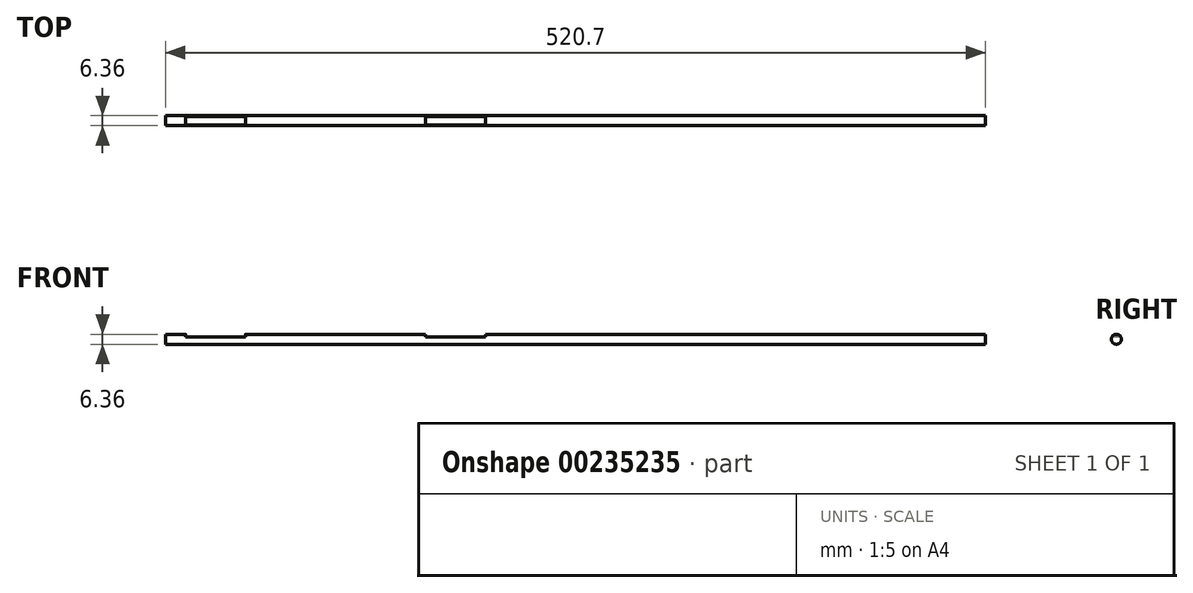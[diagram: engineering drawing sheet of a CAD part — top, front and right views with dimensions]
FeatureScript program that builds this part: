
annotation { "Feature Type Name" : "Feature", "Feature Type Description" : "" }
export const myFeature = defineFeature(function(context is Context, id is Id, definition is map)
    precondition{}
    {
        {
            var Q0;
            Q0=qCreatedBy(makeId("Right.planeOp"),FACE);
            var sketch = newSketch(context, id + "F0", { "sketchPlane" : qUnion([Q0])});
            skCircle(sketch, "E0", {"center": v(0, 0) * mm, "radius": 3.18 * mm});
            skSolve(sketch);
        }
        {
            var Q0;
            Q0=makeQuery(id+"F0.imprint","IMPRINT",FACE,{"disambiguationData":[TD([[makeQuery(id+"F0.imprint","IMPRINT",EDGE,{"derivedFrom":sQuery(id+"F0.wireOp",EDGE,"E0")}),1.0]])]});
            var Q1;
            Q1=sQuery(id+"F0.wireOp",EDGE,"E0");
            extrude(context, id + "F1", {"entities" : qUnion([Q0]), "surfaceEntities" : qUnion([Q1]), "endBound" : BoundingType.SYMMETRIC, "depth" : 520.7 * mm});
        }
        {
            var Q0;
            Q0=qCreatedBy(makeId("Front.planeOp"),FACE);
            var sketch = newSketch(context, id + "F2", { "sketchPlane" : qUnion([Q0])});
            skLineSegment(sketch, "E1.bottom", {"start": v(-247.65, 1.59) * mm, "end": v(-209.55, 1.59) * mm});
            skLineSegment(sketch, "E1.top", {"start": v(-247.65, 6.67) * mm, "end": v(-209.55, 6.67) * mm});
            skLineSegment(sketch, "E1.left", {"start": v(-247.65, 1.59) * mm, "end": v(-247.65, 6.67) * mm});
            skLineSegment(sketch, "E1.right", {"start": v(-209.55, 1.59) * mm, "end": v(-209.55, 6.67) * mm});
            skSolve(sketch);
        }
        {
            var Q0;
            Q0=makeQuery(id+"F2.imprint","IMPRINT",FACE,{"disambiguationData":[TD([[makeQuery(id+"F2.imprint","IMPRINT",EDGE,{"derivedFrom":sQuery(id+"F2.wireOp",EDGE,"E1.bottom")}),1.0]])]});
            extrude(context, id + "F3", {"entities" : qUnion([Q0]), "operationType" : NewBodyOperationType.REMOVE, "endBound" : BoundingType.SYMMETRIC, "oppositeDirection" : true, "depth" : 25.4 * mm});
        }
        {
            var Q0;
            Q0=qCreatedBy(makeId("Front.planeOp"),FACE);
            var sketch = newSketch(context, id + "F4", { "sketchPlane" : qUnion([Q0])});
            skLineSegment(sketch, "E2.bottom", {"start": v(-95.25, 1.59) * mm, "end": v(-57.15, 1.59) * mm});
            skLineSegment(sketch, "E2.top", {"start": v(-95.25, 6.67) * mm, "end": v(-57.15, 6.67) * mm});
            skLineSegment(sketch, "E2.left", {"start": v(-95.25, 1.59) * mm, "end": v(-95.25, 6.67) * mm});
            skLineSegment(sketch, "E2.right", {"start": v(-57.15, 1.59) * mm, "end": v(-57.15, 6.67) * mm});
            skSolve(sketch);
        }
        {
            var Q0;
            Q0 = qSketchRegion(id + "F4", true);
            extrude(context, id + "F5", {"entities" : qUnion([Q0]), "operationType" : NewBodyOperationType.REMOVE, "endBound" : BoundingType.SYMMETRIC, "depth" : 25.4 * mm});
        }
    });
